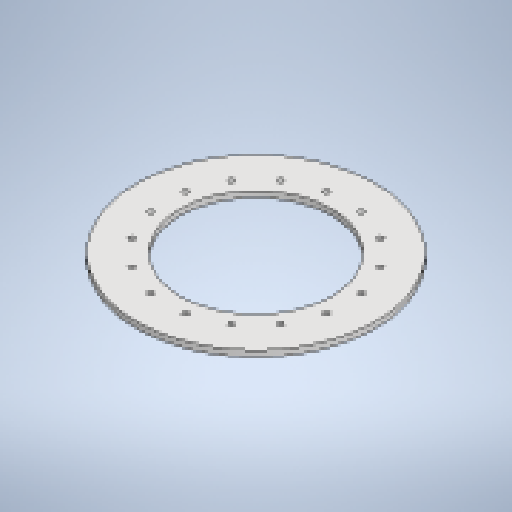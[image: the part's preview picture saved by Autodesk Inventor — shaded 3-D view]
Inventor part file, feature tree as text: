
AUTODESK INVENTOR PART (.ipt)
format: ipt  version: 2025 (Build 290162010, 162A)  size: 219,136 bytes
history: native  units: mm
features: extrude x2, sketch x2, pattern_circular x1, other x1
ambient origin geometry x8: Origin, YZ Plane, XZ Plane, XY Plane, X Axis, Y Axis, Z Axis, Center Point
bodies: Solid1 (feature_tree)
feature tree (6):
  extrude  "Extrusion1"  TaperAngle=0.0deg  [1 undecoded]
  extrude  "Extrusion3"  Depth=14.0mm
  pattern_circular  "Circular Pattern2"  Count=16 Angle=360.0deg
  sketch  "Sketch1"  dims[d2=15.0mm d3=0.0mm d10=0.0mm d11=0.0mm]
  sketch  "Sketch3"  dims[d20=1.963495mm d21=14.0mm d22=160.0mm d23=360.0deg d41=600.0mm d42=380.0mm d43=450.0mm]
  other  "Definition1"
note: 1 required parameter value undecoded (feature->parameter linkage not recoverable at this tier; creation-order binding heuristic only, values carry confidence <= 0.55)
